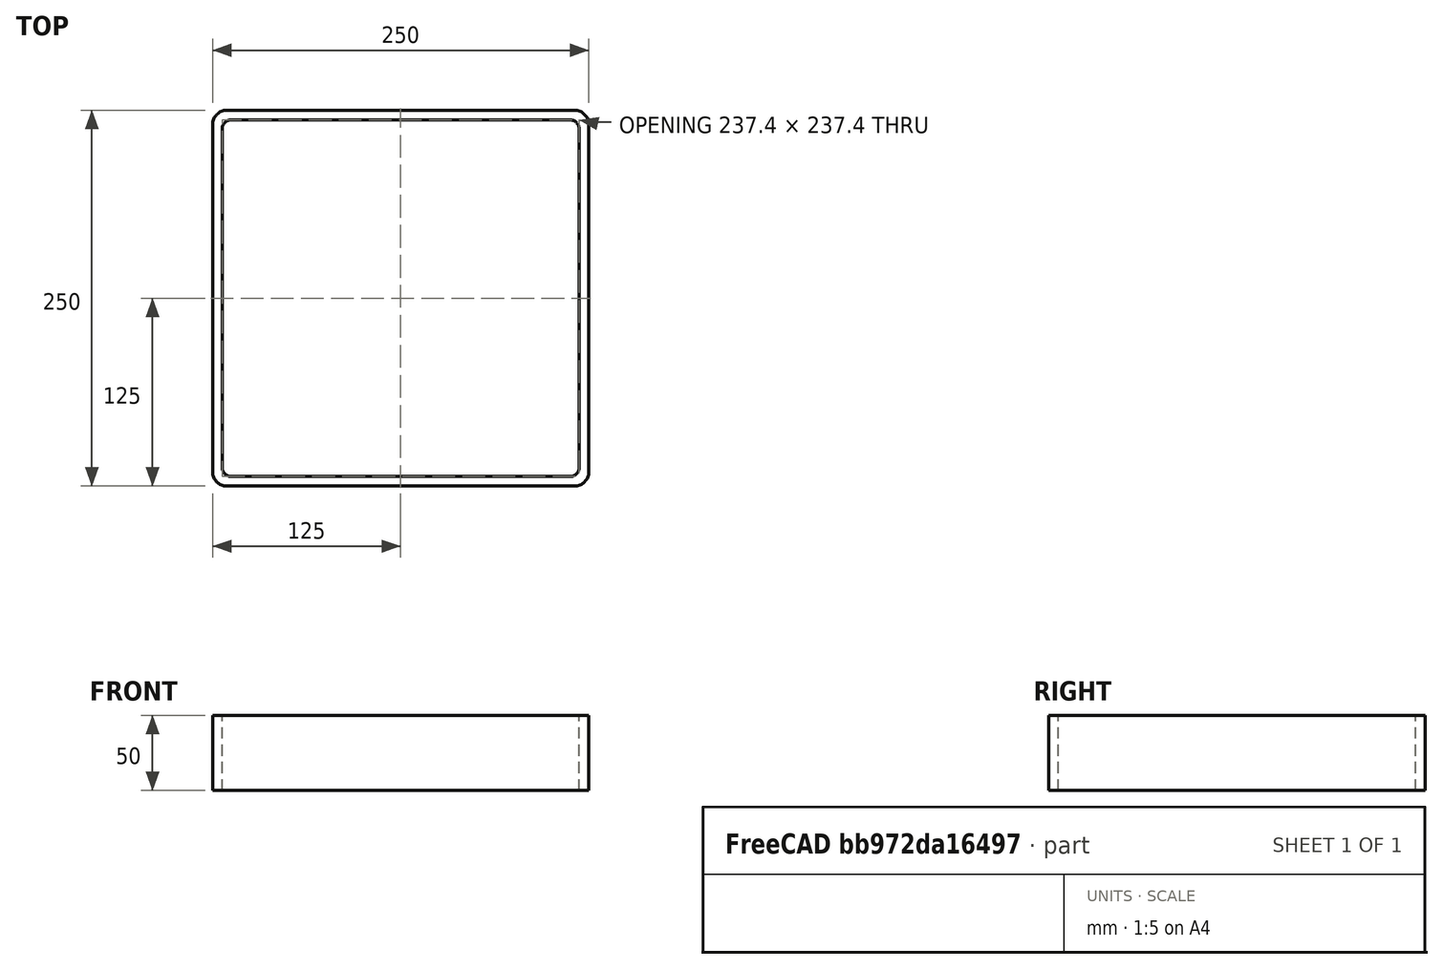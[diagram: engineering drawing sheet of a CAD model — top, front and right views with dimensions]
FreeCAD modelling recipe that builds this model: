
FCSTD DOCUMENT  (FreeCAD 0.15R4671 (Git))
Label: Square hollow section 250x250x6.3 EN10219 S235JRH
License: All rights reserved
LicenseURL: http://en.wikipedia.org/wiki/All_rights_reserved
objects: Sketcher::SketchObject×1, Part::Extrusion×1
note: 2 computed .brp shape members not serialized (recipe doc carries the construction recipe); baked Part::Feature solids carry a one-line shape summary decoded from their .brp

FEATURE [Sketcher::SketchObject] Sketch
  sketch-geometry (16):
    g0: LineSegment StartX=-112.4 StartY=118.7 StartZ=0 EndX=112.4 EndY=118.7 EndZ=0
    g1: LineSegment StartX=118.7 StartY=112.4 StartZ=0 EndX=118.7 EndY=-112.4 EndZ=0
    g2: LineSegment StartX=112.4 StartY=-118.7 StartZ=0 EndX=-112.4 EndY=-118.7 EndZ=0
    g3: LineSegment StartX=-118.7 StartY=-112.4 StartZ=0 EndX=-118.7 EndY=112.4 EndZ=0
    g4: LineSegment StartX=-115.55 StartY=125 StartZ=0 EndX=115.55 EndY=125 EndZ=0
    g5: LineSegment StartX=125 StartY=115.55 StartZ=0 EndX=125 EndY=-115.55 EndZ=0
    g6: LineSegment StartX=115.55 StartY=-125 StartZ=0 EndX=-115.55 EndY=-125 EndZ=0
    g7: LineSegment StartX=-125 StartY=-115.55 StartZ=0 EndX=-125 EndY=115.55 EndZ=0
    g8: ArcOfCircle CenterX=-112.4 CenterY=112.4 CenterZ=0 NormalX=0 NormalY=0 NormalZ=1 Radius=6.3 StartAngle=1.5708 EndAngle=3.14159
    g9: ArcOfCircle CenterX=112.4 CenterY=112.4 CenterZ=0 NormalX=0 NormalY=0 NormalZ=1 Radius=6.3 StartAngle=0 EndAngle=1.5708
    g10: ArcOfCircle CenterX=112.4 CenterY=-112.4 CenterZ=0 NormalX=0 NormalY=0 NormalZ=1 Radius=6.3 StartAngle=4.71239 EndAngle=6.28319
    g11: ArcOfCircle CenterX=-112.4 CenterY=-112.4 CenterZ=0 NormalX=0 NormalY=0 NormalZ=1 Radius=6.3 StartAngle=3.14159 EndAngle=4.71239
    g12: ArcOfCircle CenterX=115.55 CenterY=115.55 CenterZ=0 NormalX=0 NormalY=0 NormalZ=1 Radius=9.45 StartAngle=0 EndAngle=1.5708
    g13: ArcOfCircle CenterX=115.55 CenterY=-115.55 CenterZ=0 NormalX=0 NormalY=0 NormalZ=1 Radius=9.45 StartAngle=4.71239 EndAngle=6.28319
    g14: ArcOfCircle CenterX=-115.55 CenterY=-115.55 CenterZ=0 NormalX=0 NormalY=0 NormalZ=1 Radius=9.45 StartAngle=3.14159 EndAngle=4.71239
    g15: ArcOfCircle CenterX=-115.55 CenterY=115.55 CenterZ=0 NormalX=0 NormalY=0 NormalZ=1 Radius=9.45 StartAngle=1.5708 EndAngle=3.14159
  constraints (36):
    c: Horizontal(g2)
    c: Vertical(g3)
    c: Horizontal(g6)
    c: Vertical(g7)
    c: Tangent(g3,g8) = 1.5708
    c: Tangent(g0,g8) = 1.5708
    c: Tangent(g0,g9) = 1.5708
    c: Tangent(g1,g9) = 1.5708
    c: Tangent(g1,g10) = 1.5708
    c: Tangent(g2,g10) = 1.5708
    c: Tangent(g2,g11) = 1.5708
    c: Tangent(g3,g11) = 1.5708
    c: Tangent(g4,g12) = 1.5708
    c: Tangent(g5,g12) = 1.5708
    c: Tangent(g5,g13) = 1.5708
    c: Tangent(g6,g13) = 1.5708
    c: Tangent(g6,g14) = 1.5708
    c: Tangent(g7,g14) = 1.5708
    c: Tangent(g7,g15) = 1.5708
    c: Tangent(g4,g15) = 1.5708
    c: Equal(g9,g8)
    c: Equal(g9,g11)
    c: Equal(g9,g10)
    c: Equal(g12,g15)
    c: Equal(g12,g14)
    c: Equal(g12,g13)
    c: Symmetric(g4,g6,g-1)
    c: Symmetric(g7,g5,g-2)
    c: DistanceY(g4,g6) = -250
    c: DistanceX(g7,g5) = 250
    c: Symmetric(g3,g1,g-2)
    c: Symmetric(g0,g2,g-1)
    c: DistanceY(g0,g4) = 6.3
    c: DistanceX(g5,g1) = -6.3
    c: Radius(g9) = 6.3
    c: Radius(g12) = 9.45
FEATURE [Part::Extrusion] Extrude  label="Square hollow section 250x250x6.3 EN10219 S235JRH"
  Base = -> Sketch
  Dir = (0,0,50)
  Solid = true
